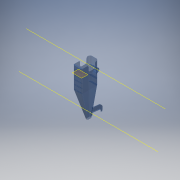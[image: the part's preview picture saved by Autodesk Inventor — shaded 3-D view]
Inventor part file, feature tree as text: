
AUTODESK INVENTOR PART (.ipt)
format: ipt  version: 2017 (Build 210142000, 142)  size: 1,044,992 bytes
history: native  units: mm
features: sketch x22, extrude x10, fillet x7, plane x6, projected_geometry x6, other x5, pattern_linear x3, loft x2, sweep x2, shell x1, hole x1
ambient origin geometry x8: Origin, YZ Plane, XZ Plane, XY Plane, X Axis, Y Axis, Z Axis, Center Point
bodies: Solid1 (feature_tree)
feature tree (65):
  plane  "Work Plane1"
  sketch  "Sketch1"  dims[d1=1200.0mm d2=600.0mm]
  plane  "Work Plane2"
  sketch  "Sketch2"  dims[d3=100.0mm d4=150.0mm]
  plane  "Work Plane3"
  sketch  "Sketch3"  dims[d5=50.0mm d6=300.0mm d7=150.0mm d8=200.0mm]
  sketch  "Sketch4"  dims[d10=0.0mm d11=90.0deg d12=0.0mm d13=90.0deg d41=150.0mm d42=300.0mm]
  loft  "Loft1"
  loft  "Loft2"
  extrude  "Extrusion4"  Depth=300.0mm
  fillet  "Fillet7"  Radius=150.0mm
  fillet  "Fillet8"  Radius=200.0mm
  fillet  "Fillet9"  Radius=150.0mm
  fillet  "Fillet10"  Radius=300.0mm
  sketch  "Sketch15"  dims[d52=200.0mm d53=0.0mm d54=150.0mm d55=50.0mm]
  plane  "Work Plane7"
  extrude  "Extrusion9"  Depth=200.0mm
  extrude  "Extrusion10"  TaperAngle=0.0deg  [1 undecoded]
  plane  "Work Plane8"
  sweep  "Sweep1"
  extrude  "Extrusion11"  Depth=150.0mm
  shell  "Shell3"  Thickness=50.0mm
  extrude  "Extrusion14"  Depth=5.0mm
  sketch  "Sketch27"  dims[d122=800.0mm d123=0.0mm d124=-100.0mm]
  sketch  "Sketch28"  dims[d125=100.0mm d126=3400.0mm d127=150.0mm]
  sweep  "Sweep2"
  extrude  "Extrusion15"  [1 undecoded]
  other  "Work Axis1"
  other  "Work Axis2"
  extrude  "Extrusion16"  Depth=35.0mm
  pattern_linear  "Rectangular Pattern1"  Count1=14  [1 undecoded]
  extrude  "Extrusion17"  Depth=12.829032mm
  fillet  "Fillet16"  Radius=800.0mm
  hole  "Hole1"  [1 undecoded]
  extrude  "Extrusion18"  Depth=3400.0mm
  fillet  "Fillet17"  Radius=150.0mm
  plane  "Work Plane10"
  extrude  "Extrusion19"  TaperAngle=0.0deg  [1 undecoded]
  pattern_linear  "Rectangular Pattern2"  Count1=80 Spacing1=0.0mm
  pattern_linear  "Rectangular Pattern3"  Count1=5  [1 undecoded]
  fillet  "Fillet18"  Radius=6.0mm
  sketch  "Sketch9"  dims[d43=50.0mm d44=200.0mm]
  sketch  "Sketch10"  dims[d45=0.0mm d46=90.0deg d47=0.0mm d48=90.0deg]
  projected_geometry  "Projected Loop2"
  sketch  "Sketch11"  dims[d50=300.0mm d51=750.0mm]
  projected_geometry  "Projected Loop3"
  projected_geometry  "Projected Loop6"
  sketch  "Sketch19"  dims[d56=20.0mm d57=5.0mm]
  projected_geometry  "Projected Loop11"
  sketch  "Sketch20"  dims[d58=5.0mm d71=500.0mm]
  sketch  "Sketch21"  dims[d72=50.0mm d84=-750.0mm]
  projected_geometry  "Projected Loop12"
  sketch  "Sketch22"  dims[d114=50.0mm d115=35.0mm d116=140.0mm]
  sketch  "Sketch25"  dims[d118=12.829032mm d119=12.829032mm d120=800.0mm d121=0.0mm]
  projected_geometry  "Projected Loop14"
  sketch  "3D Sketch1"
  sketch  "Sketch29"  dims[d128=600.0mm d129=0.0mm d130=0.0mm d131=800.0mm d132=0.0mm d133=50.0mm d134=6.0mm]
  sketch  "Sketch30"  dims[d143=90.0mm]
  sketch  "Sketch31"  dims[d144=60.0mm]
  sketch  "Sketch32"  dims[d145=1000.0mm d146=0.0mm]
  sketch  "Sketch33"  dims[d148=16.0mm]
  sketch  "Sketch35"  dims[d149=0.0mm d150=0.0mm d151=90.0mm d152=400.0mm d153=1000.0mm d154=0.0mm d155=6.0mm d156=0.0mm d157=60.0mm d159=300.0mm d160=60.0mm d161=60.0mm d162=60.0mm d163=60.0mm d164=60.0mm d165=50.0mm d166=100.0mm d167=100.0mm d168=100.0mm d169=100.0mm d170=1210.0mm d171=0.0mm d172=10.0mm d173=6.0mm d174=30.0mm d175=30.0mm d176=115.0mm d177=4.0mm d178=6.0mm d179=4.0mm d180=2.0mm d181=90.0deg d182=1510.0mm d183=0.0mm d184=100.0mm d185=400.0mm d186=400.0mm d187=100.0mm d188=1210.0mm d189=0.0mm d190=100.0mm d192=-500.0mm d193=6.0mm d194=0.0mm d195=20.0mm d197=600.0mm d198=20.0mm d200=1000.0mm d201=10.0mm]
  other  "<userpath>\Dropbox\CarPlane\CarPlane.iam"
  other  "CarPlane.iam"
  other  "MetricsTop:1"
note: 6 required parameter values undecoded (feature->parameter linkage not recoverable at this tier; creation-order binding heuristic only, values carry confidence <= 0.55)
